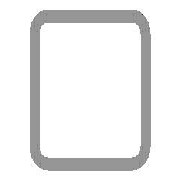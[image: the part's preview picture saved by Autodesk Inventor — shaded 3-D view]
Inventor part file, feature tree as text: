
AUTODESK INVENTOR PART (.ipt)
format: ipt  version: 2025 (Build 290162010, 162A)  size: 133,632 bytes
history: native  units: mm (DEFAULTED — no unit token found)
features: other x4, sketch x1, plane x1
ambient origin geometry x8: Origin, YZ Plane, XZ Plane, XY Plane, X Axis, Y Axis, Z Axis, Center Point
bodies: Solid1 (feature_tree), Body (feature_tree)
feature tree (6):
  parser-record x1  (decoder bookkeeping rows leaked as tree rows — omitted from the tree; the rows remain in map.json)
  other  "Driven Length"
  other  "Start Plane"
  other  "End Plane"
  sketch  "Sketch3"  dims[d3=2150.0mm d4=0.0mm d7=8.0mm d9=50.0mm d11=50.0mm d12=4.0mm d13=-0.0mm d14=2150.0mm d15=25.0mm d16=25.0mm d17=90.0deg d18=2150.0mm]
  plane  "Work Plane3"
